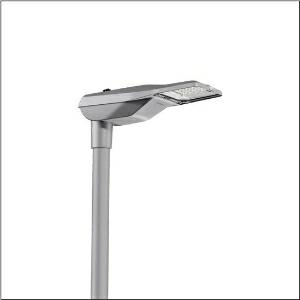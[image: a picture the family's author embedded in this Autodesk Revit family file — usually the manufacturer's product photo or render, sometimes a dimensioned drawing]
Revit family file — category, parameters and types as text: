
# Revit family: streetlight_sl_21_iq_micro___st1_0a_5xe1d31v08cb_77a3
name_source: partatom
category: Lighting Fixtures
units: mm (PartAtom-declared; Revit-internal decimal feet)

## family parameters
Cut with Voids When Loaded = No
Host = Face
Light Source = No
Part Type = Normal
Room Calculation Point = No
Round Connector Dimension = Use Diameter
Shared = No

## types (1)
- --- (1 x LED, 2880 lm, 19.1 W, 3000K)
    Apparent Load = 19 VA
    CIE Flux Codes = 37 72 97 100 100
    Color Rendering = 70
    Color Temperature = 3000K
    Default Elevation = 1800 mm
    Description = Streetlight SL 21 iQ micro, mast luminaire, primary light control with lens, of PMMA, primary optical cover: cover, of toughened safety glass, transparent, light distribution: ST1.0a, light emission: direct distribution, primary light characteristic: asymmetric, installation type: post-top, side-entry, LED, High Power LED, rated luminous flux: 2.880lm, luminous efficacy: 151lm/W, light colour: 730, colour temperature: 3000K, control gear: iQ-Street Remote, D4i with power reduction, control: pre-setting: logarithmic dimming characteristic, Street-Remote, Auto-Match, Temp-Guard, Lumen-Switch, Night-Set, Smart-Wire, Light-Fading, Desk-Remote (wireless, voltage-free reading and setting of iQ features in the workshop via application-optimized NFC function/RFID function), optimised constant luminous flux control (CLO 2.0), mains connection: 220..240V, AC, 50/60Hz, start of lifetime: 19W, end of service life: 20W, reduction: 9W, luminaire housing, of diecast aluminium, powder-coated, Siteco® metallic grey (DB 702S), corrosivity category C5 mid according to DIN EN ISO 12944, please order mast flange separately, inclination adjustable: 0°, 5°, 10°, 15°, sealing non-destructively replaceable, multi-level sealing system, length: 528mm, width: 235mm, height: 110mm, mast flange for spigot size: 42mm (side-entry): 5XC10008XM4, 60/48mm (side-entry/post-top): 5XC10108XM2, 76/60mm (side-entry/post-top): 5XC10108XM1, mounting height: 4..8m, Smart Interface above, protection rating (complete): IP66, insulation class (complete): insulation class II (safety insulation), certification: CE, ENEC, ENEC+, VDE, impact resistance: IK10, permissible operating ambient temperature for outdoor applications: -40..+50°C, standard-compliant lighting for roads and squares, packaging unit: 1 piece

Light Distribution: ST1.0a
    Height = 110 mm
    Lamp = 1 x LED
    Lamp Light Flux = 2880 lm
    Lamp Power = 19.1 W
    Lamp count = 1
    Length = 528 mm
    Luminous efficacy = 151 lm/W
    Manufacturer = Siteco
    ModVariant = No
    Model = 5XE1D31V08CB
    Number of Poles = 1
    OnlyDefault = Yes
    Power Factor = 1
    Product Name = Streetlight SL 21 iQ micro | ST1.0a
    Product group = mast luminaire | pylon top
    ProductGroupID = 6100
    Protection Class = Protection class II
    Protection Degree = IP 66
    RLX_Detail_Level = 1
    RLX_Emergency_Light_Flux = 0 lm
    RLX_Emergency_Type = 0
    RLX_Emergency_Type_DB = No
    RlxData = <blob elided: 98357 chars, md5=98a813ba>
    Socket = socket
    Standby Power = 0 W
    System Light Flux = 2880 lm
    System Power = 19 W
    Type Comments = factory setting: luminous flux: 100 % | dim-lin: 254 | 387 mA
    Type Image = l_1277292.jpg
    URL = http://relux.com
    VarID = @adj_115684
    Voltage = 0 V
    Weight = 0.00 kg
    Width = 235 mm

## geometry (parser evidence)
native form markers: Blend x4, Sweep x12
no freeform markers — native parametric forms only
